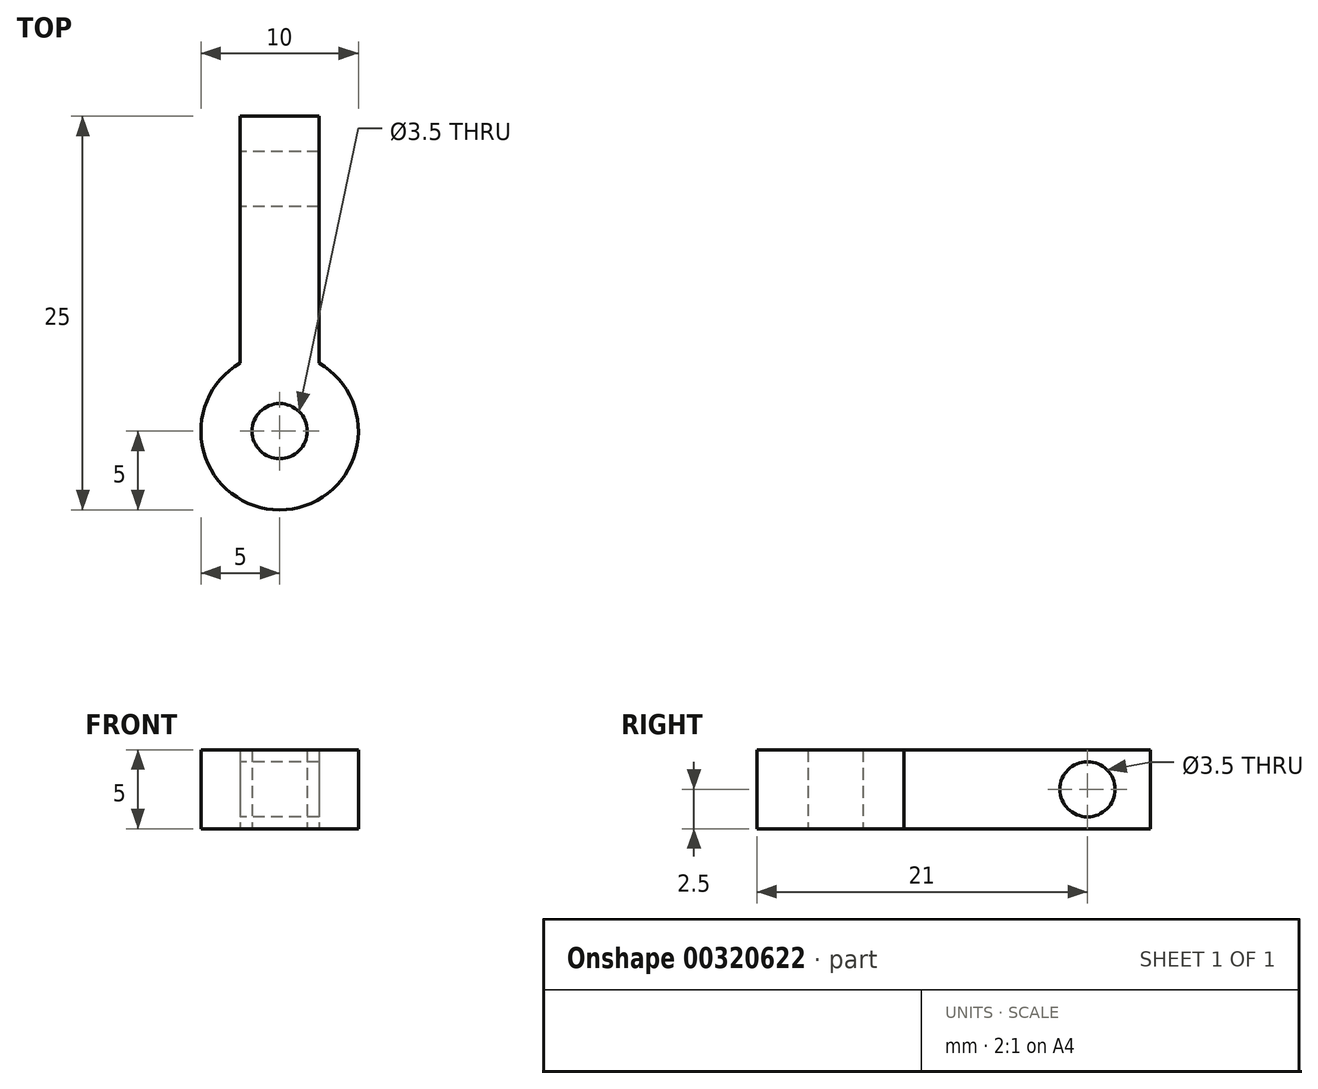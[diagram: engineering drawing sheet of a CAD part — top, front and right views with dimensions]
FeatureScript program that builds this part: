
annotation { "Feature Type Name" : "Feature", "Feature Type Description" : "" }
export const myFeature = defineFeature(function(context is Context, id is Id, definition is map)
    precondition{}
    {
        {
            var Q0;
            Q0=qCreatedBy(makeId("Top.planeOp"),FACE);
            var sketch = newSketch(context, id + "F0", { "sketchPlane" : qUnion([Q0])});
            skLineSegment(sketch, "E0.top", {"start": v(2.5, 10) * mm, "end": v(-2.5, 10) * mm});
            skLineSegment(sketch, "E0.left", {"start": v(2.5, -5.67) * mm, "end": v(2.5, 10) * mm});
            skLineSegment(sketch, "E0.right", {"start": v(-2.5, -5.67) * mm, "end": v(-2.5, 10) * mm});
            skPoint(sketch, "E0.middle", {"position": v(0, 0) * mm});
            skArc(sketch, "E1", {"start": v(-2.5, -5.67) * mm, "mid": v(0, -15) * mm, "end": v(2.5, -5.67) * mm});
            skPoint(sketch, "E2.orphan", {"position": v(-2.5, -10) * mm});
            skPoint(sketch, "E3.orphan", {"position": v(2.5, -10) * mm});
            skCircle(sketch, "E4", {"center": v(0, -10) * mm, "radius": 1.75 * mm});
            skSolve(sketch);
        }
        {
            var Q0;
            Q0 = qSketchRegion(id + "F0", true);
            extrude(context, id + "F1", {"entities" : qUnion([Q0]), "depth" : 5 * mm});
        }
        {
            var Q0;
            Q0=makeQuery(id+"F1.opExtrude","SWEPT_FACE",FACE,{"disambiguationData":[OSD([sQuery(id+"F0.wireOp",EDGE,"E0.right")])]});
            var sketch = newSketch(context, id + "F2", { "sketchPlane" : qUnion([Q0])});
            skLineSegment(sketch, "E5", {"start": v(-10, 2.5) * mm, "end": v(-6, 2.5) * mm, "construction": true});
            skCircle(sketch, "E6", {"center": v(-6, 2.5) * mm, "radius": 1.75 * mm});
            skSolve(sketch);
        }
        {
            var Q0;
            Q0=makeQuery(id+"F2.imprint","IMPRINT",FACE,{"disambiguationData":[TD([[makeQuery(id+"F2.imprint","IMPRINT",EDGE,{"derivedFrom":sQuery(id+"F2.wireOp",EDGE,"E6")}),1.0]])]});
            var Q1;
            Q1=sQuery(id+"F2.wireOp",EDGE,"E6");
            extrude(context, id + "F3", {"entities" : qUnion([Q0]), "operationType" : NewBodyOperationType.REMOVE, "surfaceEntities" : qUnion([Q1]), "oppositeDirection" : true, "depth" : 25 * mm});
        }
    });
